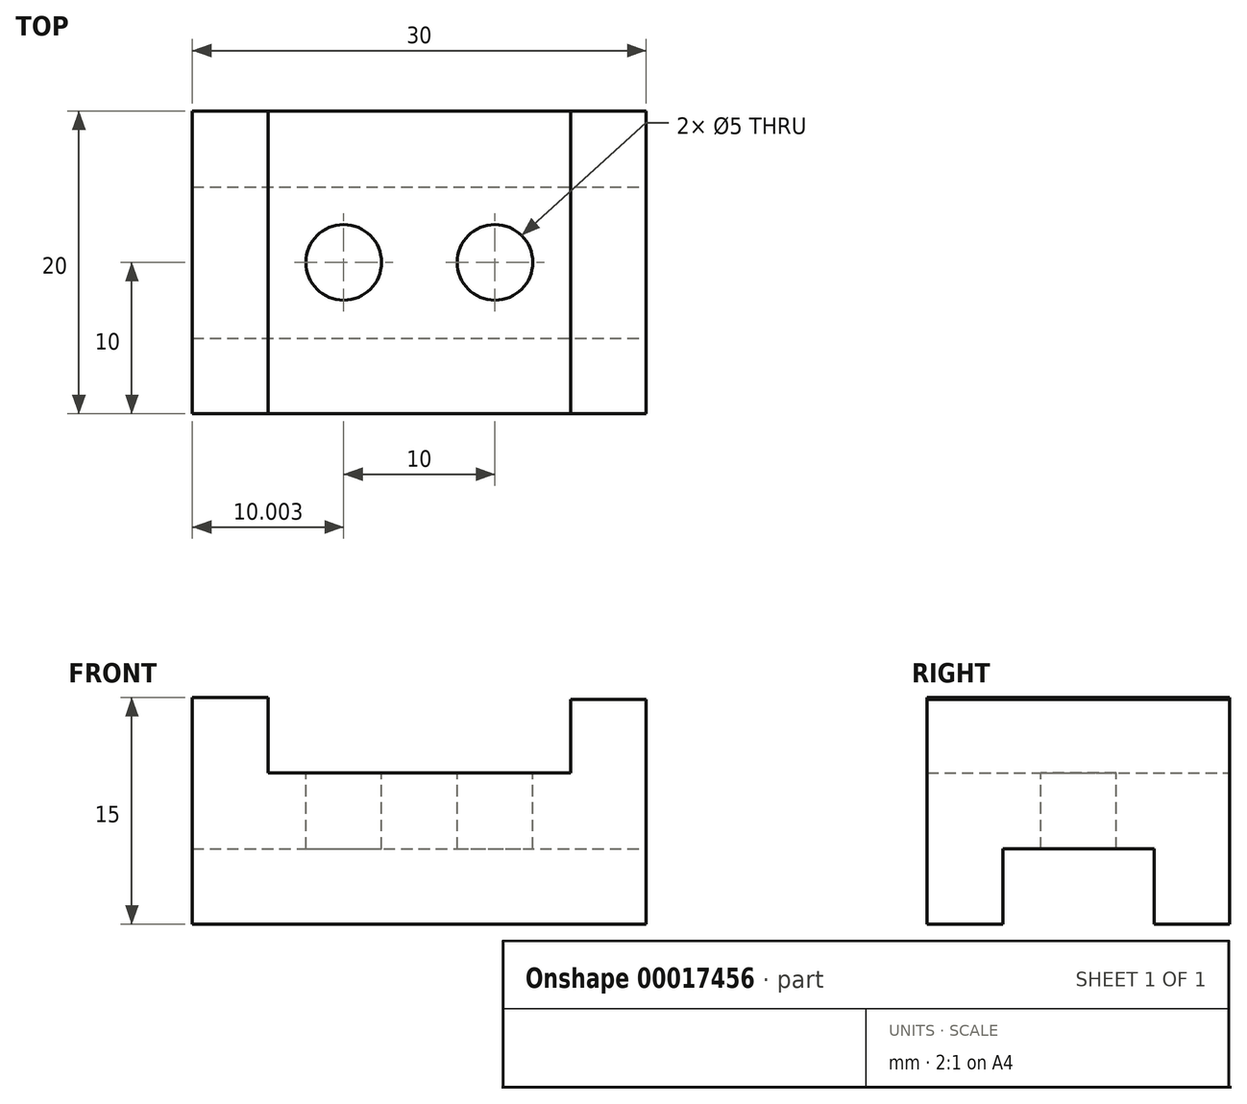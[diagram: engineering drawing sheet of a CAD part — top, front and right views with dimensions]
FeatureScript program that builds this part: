
annotation { "Feature Type Name" : "Feature", "Feature Type Description" : "" }
export const myFeature = defineFeature(function(context is Context, id is Id, definition is map)
    precondition{}
    {
        {
            var Q0;
            Q0=qCreatedBy(makeId("Front.planeOp"),FACE);
            var sketch = newSketch(context, id + "F0", { "sketchPlane" : qUnion([Q0])});
            skLineSegment(sketch, "E0", {"start": v(-21.75, 15) * mm, "end": v(-16.75, 15) * mm});
            skLineSegment(sketch, "E1", {"start": v(-21.75, 15) * mm, "end": v(-21.75, 0) * mm});
            skLineSegment(sketch, "E2", {"start": v(-21.75, 0) * mm, "end": v(8.25, 0) * mm});
            skLineSegment(sketch, "E3", {"start": v(-16.75, 15) * mm, "end": v(-16.75, 10) * mm});
            skLineSegment(sketch, "E4", {"start": v(-16.75, 10) * mm, "end": v(3.25, 10) * mm});
            skLineSegment(sketch, "E5", {"start": v(8.25, 0) * mm, "end": v(8.25, 14.87) * mm});
            skLineSegment(sketch, "E6", {"start": v(8.25, 14.87) * mm, "end": v(3.25, 14.87) * mm});
            skLineSegment(sketch, "E7", {"start": v(3.25, 14.87) * mm, "end": v(3.25, 10) * mm});
            skSolve(sketch);
        }
        {
            var Q0;
            Q0 = qSketchRegion(id + "F0", true);
            var Q1;
            Q1 = qSketchRegion(id + "F4", true);
            extrude(context, id + "F1", {"entities" : qUnion([Q0, Q1]), "depth" : 20 * mm});
        }
        {
            var Q0;
            Q0=makeQuery(id+"F1.opExtrude","SWEPT_FACE",FACE,{"disambiguationData":[OSD([sQuery(id+"F0.wireOp",EDGE,"E5")])]});
            var sketch = newSketch(context, id + "F2", { "sketchPlane" : qUnion([Q0])});
            skLineSegment(sketch, "E8", {"start": v(-15, 0) * mm, "end": v(-15, 5) * mm});
            skLineSegment(sketch, "E9", {"start": v(-15, 5) * mm, "end": v(-5, 5) * mm});
            skLineSegment(sketch, "E10", {"start": v(-5, 5) * mm, "end": v(-5, 0) * mm});
            skSolve(sketch);
        }
        {
            var Q0;
            {var subQ2=sQuery(id+"F2.wireOp",EDGE,"E8");Q0=makeQuery(id+"F2.imprint","IMPRINT",FACE,{"disambiguationData":[TD([[makeQuery(id+"F2.imprint","IMPRINT",EDGE,{"derivedFrom":subQ2}),-1.0]])]});}
            extrude(context, id + "F3", {"entities" : qUnion([Q0]), "operationType" : NewBodyOperationType.REMOVE, "endBound" : BoundingType.THROUGH_ALL, "oppositeDirection" : true, "depth" : 25 * mm});
        }
        {
            var Q0;
            Q0=makeQuery(id+"F1.opExtrude","SWEPT_FACE",FACE,{"disambiguationData":[OSD([sQuery(id+"F0.wireOp",EDGE,"E4")])]});
            var sketch = newSketch(context, id + "F4", { "sketchPlane" : qUnion([Q0])});
            skCircle(sketch, "E11", {"center": v(-11.75, -10) * mm, "radius": 2.5 * mm});
            skCircle(sketch, "E12", {"center": v(-1.75, -10) * mm, "radius": 2.5 * mm});
            skSolve(sketch);
        }
        {
            var Q0;
            Q0 = qSketchRegion(id + "F4", true);
            extrude(context, id + "F5", {"entities" : qUnion([Q0]), "operationType" : NewBodyOperationType.REMOVE, "oppositeDirection" : true, "depth" : 10 * mm});
        }
    });
